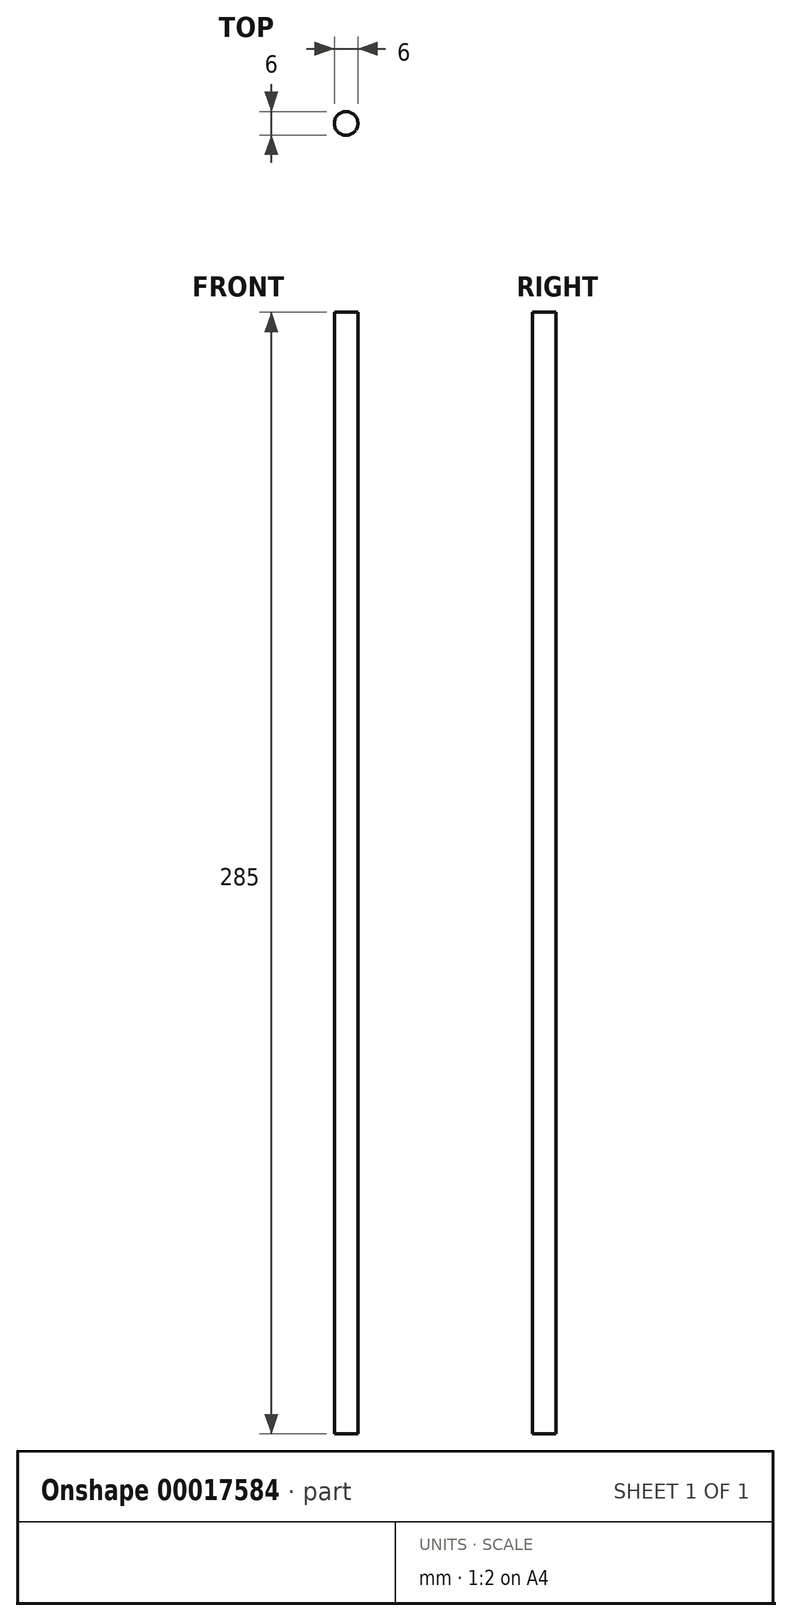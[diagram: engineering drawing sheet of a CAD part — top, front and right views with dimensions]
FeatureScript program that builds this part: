
annotation { "Feature Type Name" : "Feature", "Feature Type Description" : "" }
export const myFeature = defineFeature(function(context is Context, id is Id, definition is map)
    precondition{}
    {
        {
            var Q0;
            Q0=qCreatedBy(makeId("Top.planeOp"),FACE);
            var sketch = newSketch(context, id + "F0", { "sketchPlane" : qUnion([Q0])});
            skCircle(sketch, "E0", {"center": v(0, 0) * mm, "radius": 3 * mm});
            skSolve(sketch);
        }
        {
            var Q0;
            Q0=qSketchRegion(id+"F0",true);
            extrude(context, id + "F1", {"entities" : qUnion([Q0]), "depth" : 285 * mm});
        }
    });
